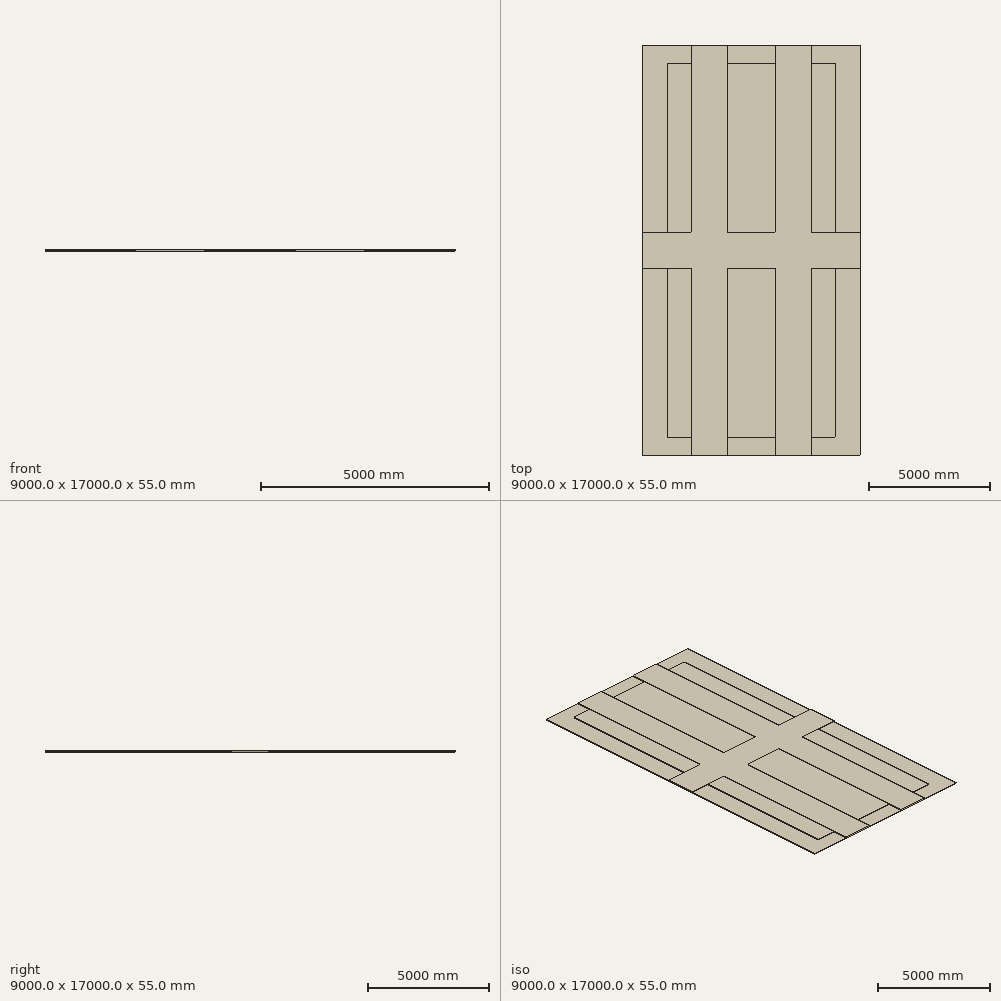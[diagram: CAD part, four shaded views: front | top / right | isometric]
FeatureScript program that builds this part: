
annotation { "Feature Type Name" : "Feature", "Feature Type Description" : "" }
export const myFeature = defineFeature(function(context is Context, id is Id, definition is map)
    precondition{}
    {
        {
            var Q0;
            Q0=qCreatedBy(makeId("Top.planeOp"),FACE);
            var sketch = newSketch(context, id + "F0", { "sketchPlane" : qUnion([Q0])});
            skLineSegment(sketch, "E0.bottom", {"start": v(0, 0) * mm, "end": v(-9000, 0) * mm});
            skLineSegment(sketch, "E0.top", {"start": v(0, 17000) * mm, "end": v(-9000, 17000) * mm});
            skLineSegment(sketch, "E0.left", {"start": v(0, 0) * mm, "end": v(0, 17000) * mm});
            skLineSegment(sketch, "E0.right", {"start": v(-9000, 0) * mm, "end": v(-9000, 17000) * mm});
            skSolve(sketch);
        }
        {
            var Q0;
            Q0=makeQuery(id+"F0.imprint","IMPRINT",FACE,{"disambiguationData":[TD([[makeQuery(id+"F0.imprint","IMPRINT",EDGE,{"derivedFrom":sQuery(id+"F0.wireOp",EDGE,"E0.bottom")}),-1.0]])]});
            extrude(context, id + "F1", {"entities" : qUnion([Q0]), "depth" : 25 * mm, "offsetDistance" : 25 * mm});
        }
        {
            var Q0;
            Q0=makeQuery(id+"F1.opExtrude","CAP_FACE",FACE,{"disambiguationData":[OSD([sQuery(id+"F0.wireOp",EDGE,"E0.bottom"),sQuery(id+"F0.wireOp",EDGE,"E0.top"),sQuery(id+"F0.wireOp",EDGE,"E0.left"),sQuery(id+"F0.wireOp",EDGE,"E0.right")])],"isStart":false});
            var sketch = newSketch(context, id + "F2", { "sketchPlane" : qUnion([Q0])});
            skLineSegment(sketch, "E1", {"start": v(0, 0) * mm, "end": v(-1000, 0) * mm});
            skLineSegment(sketch, "E2", {"start": v(-1000, 0) * mm, "end": v(-2000, 0) * mm});
            skLineSegment(sketch, "E3", {"start": v(-2000, 0) * mm, "end": v(-3500, 0) * mm});
            skLineSegment(sketch, "E4", {"start": v(-3500, 0) * mm, "end": v(-4500, 0) * mm});
            skLineSegment(sketch, "E5", {"start": v(-4500, 0) * mm, "end": v(-5500, 0) * mm});
            skLineSegment(sketch, "E6", {"start": v(-5500, 0) * mm, "end": v(-7000, 0) * mm});
            skLineSegment(sketch, "E7", {"start": v(-7000, 0) * mm, "end": v(-8000, 0) * mm});
            skLineSegment(sketch, "E8", {"start": v(-8000, 0) * mm, "end": v(-9000, 0) * mm});
            skLineSegment(sketch, "E9", {"start": v(-1000, 0) * mm, "end": v(-1000, 17000) * mm});
            skLineSegment(sketch, "E10", {"start": v(-2000, 0) * mm, "end": v(-2000, 17000) * mm});
            skLineSegment(sketch, "E11", {"start": v(-3500, 0) * mm, "end": v(-3500, 17000) * mm});
            skLineSegment(sketch, "E12", {"start": v(-4500, 0) * mm, "end": v(-4500, 17000) * mm});
            skLineSegment(sketch, "E13", {"start": v(-5500, 0) * mm, "end": v(-5500, 17000) * mm});
            skLineSegment(sketch, "E14", {"start": v(-7000, 0) * mm, "end": v(-7000, 17000) * mm});
            skLineSegment(sketch, "E15", {"start": v(-8000, 0) * mm, "end": v(-8000, 17000) * mm});
            skLineSegment(sketch, "E16", {"start": v(0, 0) * mm, "end": v(0, 750) * mm});
            skLineSegment(sketch, "E17", {"start": v(0, 750) * mm, "end": v(0, 7750) * mm});
            skLineSegment(sketch, "E18", {"start": v(0, 7750) * mm, "end": v(0, 9250) * mm});
            skLineSegment(sketch, "E19", {"start": v(0, 9250) * mm, "end": v(0, 16250) * mm});
            skLineSegment(sketch, "E20", {"start": v(0, 16250) * mm, "end": v(0, 17000) * mm});
            skLineSegment(sketch, "E21", {"start": v(0, 750) * mm, "end": v(-9000, 750) * mm});
            skLineSegment(sketch, "E22", {"start": v(0, 7750) * mm, "end": v(-9000, 7750) * mm});
            skLineSegment(sketch, "E23", {"start": v(0, 9250) * mm, "end": v(-9000, 9250) * mm});
            skLineSegment(sketch, "E24", {"start": v(0, 16250) * mm, "end": v(-9000, 16250) * mm});
            skSolve(sketch);
        }
        {
            var Q0;
            {var subQ0=sQuery(id+"F2.wireOp",EDGE,"E23");var subQ1=sQuery(id+"F2.wireOp",EDGE,"E14");var subQ2=makeQuery(id+"F2.imprint","INTERSECT",VERTEX,{"derivedFrom":[subQ1,subQ0]});Q0=makeQuery(id+"F2.imprint","IMPRINT",FACE,{"disambiguationData":[TD([[makeQuery(id+"F2.imprint","IMPRINT",EDGE,{"disambiguationData":[TD([[subQ2,-1.0]])],"derivedFrom":subQ1}),1.0]])]});}
            var Q1;
            {var subQ0=sQuery(id+"F2.wireOp",EDGE,"E23");var subQ1=sQuery(id+"F2.wireOp",EDGE,"E12");var subQ2=makeQuery(id+"F2.imprint","INTERSECT",VERTEX,{"derivedFrom":[subQ1,subQ0]});Q1=makeQuery(id+"F2.imprint","IMPRINT",FACE,{"disambiguationData":[TD([[makeQuery(id+"F2.imprint","IMPRINT",EDGE,{"disambiguationData":[TD([[subQ2,-1.0]])],"derivedFrom":subQ1}),1.0]])]});}
            var Q2;
            {var subQ0=sQuery(id+"F2.wireOp",EDGE,"E23");var subQ1=sQuery(id+"F2.wireOp",EDGE,"E11");var subQ2=makeQuery(id+"F2.imprint","INTERSECT",VERTEX,{"derivedFrom":[subQ1,subQ0]});Q2=makeQuery(id+"F2.imprint","IMPRINT",FACE,{"disambiguationData":[TD([[makeQuery(id+"F2.imprint","IMPRINT",EDGE,{"disambiguationData":[TD([[subQ2,-1.0]])],"derivedFrom":subQ1}),1.0]])]});}
            var Q3;
            {var subQ0=sQuery(id+"F2.wireOp",EDGE,"E23");var subQ1=sQuery(id+"F2.wireOp",EDGE,"E9");var subQ2=makeQuery(id+"F2.imprint","INTERSECT",VERTEX,{"derivedFrom":[subQ1,subQ0]});Q3=makeQuery(id+"F2.imprint","IMPRINT",FACE,{"disambiguationData":[TD([[makeQuery(id+"F2.imprint","IMPRINT",EDGE,{"disambiguationData":[TD([[subQ2,-1.0]])],"derivedFrom":subQ1}),1.0]])]});}
            var Q4;
            {var subQ0=sQuery(id+"F2.wireOp",EDGE,"E21");var subQ1=sQuery(id+"F2.wireOp",EDGE,"E14");var subQ2=makeQuery(id+"F2.imprint","INTERSECT",VERTEX,{"derivedFrom":[subQ1,subQ0]});Q4=makeQuery(id+"F2.imprint","IMPRINT",FACE,{"disambiguationData":[TD([[makeQuery(id+"F2.imprint","IMPRINT",EDGE,{"disambiguationData":[TD([[subQ2,-1.0]])],"derivedFrom":subQ1}),1.0]])]});}
            var Q5;
            {var subQ0=sQuery(id+"F2.wireOp",EDGE,"E21");var subQ1=sQuery(id+"F2.wireOp",EDGE,"E12");var subQ2=makeQuery(id+"F2.imprint","INTERSECT",VERTEX,{"derivedFrom":[subQ1,subQ0]});Q5=makeQuery(id+"F2.imprint","IMPRINT",FACE,{"disambiguationData":[TD([[makeQuery(id+"F2.imprint","IMPRINT",EDGE,{"disambiguationData":[TD([[subQ2,-1.0]])],"derivedFrom":subQ1}),1.0]])]});}
            var Q6;
            {var subQ0=sQuery(id+"F2.wireOp",EDGE,"E21");var subQ1=sQuery(id+"F2.wireOp",EDGE,"E11");var subQ2=makeQuery(id+"F2.imprint","INTERSECT",VERTEX,{"derivedFrom":[subQ1,subQ0]});Q6=makeQuery(id+"F2.imprint","IMPRINT",FACE,{"disambiguationData":[TD([[makeQuery(id+"F2.imprint","IMPRINT",EDGE,{"disambiguationData":[TD([[subQ2,-1.0]])],"derivedFrom":subQ1}),1.0]])]});}
            var Q7;
            {var subQ0=sQuery(id+"F2.wireOp",EDGE,"E21");var subQ1=sQuery(id+"F2.wireOp",EDGE,"E9");var subQ2=makeQuery(id+"F2.imprint","INTERSECT",VERTEX,{"derivedFrom":[subQ1,subQ0]});Q7=makeQuery(id+"F2.imprint","IMPRINT",FACE,{"disambiguationData":[TD([[makeQuery(id+"F2.imprint","IMPRINT",EDGE,{"disambiguationData":[TD([[subQ2,-1.0]])],"derivedFrom":subQ1}),1.0]])]});}
            extrude(context, id + "F3", {"entities" : qUnion([Q0, Q1, Q2, Q3, Q4, Q5, Q6, Q7]), "operationType" : NewBodyOperationType.ADD, "depth" : 25 * mm, "offsetDistance" : 25 * mm});
        }
        {
            var Q0;
            {var subQ0=sQuery(id+"F2.wireOp",EDGE,"E22");var subQ1=sQuery(id+"F2.wireOp",EDGE,"E14");var subQ2=makeQuery(id+"F2.imprint","INTERSECT",VERTEX,{"derivedFrom":[subQ1,subQ0]});Q0=makeQuery(id+"F2.imprint","IMPRINT",FACE,{"disambiguationData":[TD([[makeQuery(id+"F2.imprint","IMPRINT",EDGE,{"disambiguationData":[TD([[subQ2,-1.0]])],"derivedFrom":subQ1}),1.0]])]});}
            var Q1;
            {var subQ0=sQuery(id+"F2.wireOp",EDGE,"E22");var subQ1=sQuery(id+"F2.wireOp",EDGE,"E13");var subQ2=makeQuery(id+"F2.imprint","INTERSECT",VERTEX,{"derivedFrom":[subQ1,subQ0]});Q1=makeQuery(id+"F2.imprint","IMPRINT",FACE,{"disambiguationData":[TD([[makeQuery(id+"F2.imprint","IMPRINT",EDGE,{"disambiguationData":[TD([[subQ2,-1.0]])],"derivedFrom":subQ1}),1.0]])]});}
            var Q2;
            {var subQ0=sQuery(id+"F2.wireOp",EDGE,"E22");var subQ1=sQuery(id+"F2.wireOp",EDGE,"E12");var subQ2=makeQuery(id+"F2.imprint","INTERSECT",VERTEX,{"derivedFrom":[subQ1,subQ0]});Q2=makeQuery(id+"F2.imprint","IMPRINT",FACE,{"disambiguationData":[TD([[makeQuery(id+"F2.imprint","IMPRINT",EDGE,{"disambiguationData":[TD([[subQ2,-1.0]])],"derivedFrom":subQ1}),1.0]])]});}
            var Q3;
            {var subQ0=sQuery(id+"F2.wireOp",EDGE,"E22");var subQ1=sQuery(id+"F2.wireOp",EDGE,"E11");var subQ2=makeQuery(id+"F2.imprint","INTERSECT",VERTEX,{"derivedFrom":[subQ1,subQ0]});Q3=makeQuery(id+"F2.imprint","IMPRINT",FACE,{"disambiguationData":[TD([[makeQuery(id+"F2.imprint","IMPRINT",EDGE,{"disambiguationData":[TD([[subQ2,-1.0]])],"derivedFrom":subQ1}),1.0]])]});}
            var Q4;
            {var subQ0=sQuery(id+"F2.wireOp",EDGE,"E22");var subQ1=sQuery(id+"F2.wireOp",EDGE,"E10");var subQ2=makeQuery(id+"F2.imprint","INTERSECT",VERTEX,{"derivedFrom":[subQ1,subQ0]});Q4=makeQuery(id+"F2.imprint","IMPRINT",FACE,{"disambiguationData":[TD([[makeQuery(id+"F2.imprint","IMPRINT",EDGE,{"disambiguationData":[TD([[subQ2,-1.0]])],"derivedFrom":subQ1}),1.0]])]});}
            var Q5;
            {var subQ0=sQuery(id+"F2.wireOp",EDGE,"E22");var subQ1=sQuery(id+"F2.wireOp",EDGE,"E9");var subQ2=makeQuery(id+"F2.imprint","INTERSECT",VERTEX,{"derivedFrom":[subQ1,subQ0]});Q5=makeQuery(id+"F2.imprint","IMPRINT",FACE,{"disambiguationData":[TD([[makeQuery(id+"F2.imprint","IMPRINT",EDGE,{"disambiguationData":[TD([[subQ2,-1.0]])],"derivedFrom":subQ1}),1.0]])]});}
            var Q6;
            {var subQ5=sQuery(id+"F2.wireOp",EDGE,"E18");Q6=makeQuery(id+"F2.imprint","IMPRINT",FACE,{"disambiguationData":[TD([[makeQuery(id+"F2.imprint","IMPRINT",EDGE,{"derivedFrom":subQ5}),1.0]])]});}
            var Q7;
            {var subQ0=sQuery(id+"F2.wireOp",EDGE,"E22");var subQ1=sQuery(id+"F2.wireOp",EDGE,"E15");var subQ2=makeQuery(id+"F2.imprint","INTERSECT",VERTEX,{"derivedFrom":[subQ1,subQ0]});Q7=makeQuery(id+"F2.imprint","IMPRINT",FACE,{"disambiguationData":[TD([[makeQuery(id+"F2.imprint","IMPRINT",EDGE,{"disambiguationData":[TD([[subQ2,-1.0]])],"derivedFrom":subQ1}),1.0]])]});}
            var Q8;
            {var subQ0=sQuery(id+"F2.wireOp",EDGE,"E23");var subQ1=sQuery(id+"F2.wireOp",EDGE,"E13");var subQ2=makeQuery(id+"F2.imprint","INTERSECT",VERTEX,{"derivedFrom":[subQ1,subQ0]});Q8=makeQuery(id+"F2.imprint","IMPRINT",FACE,{"disambiguationData":[TD([[makeQuery(id+"F2.imprint","IMPRINT",EDGE,{"disambiguationData":[TD([[subQ2,-1.0]])],"derivedFrom":subQ1}),1.0]])]});}
            var Q9;
            {var subQ0=sQuery(id+"F2.wireOp",EDGE,"E23");var subQ1=sQuery(id+"F2.wireOp",EDGE,"E10");var subQ2=makeQuery(id+"F2.imprint","INTERSECT",VERTEX,{"derivedFrom":[subQ1,subQ0]});Q9=makeQuery(id+"F2.imprint","IMPRINT",FACE,{"disambiguationData":[TD([[makeQuery(id+"F2.imprint","IMPRINT",EDGE,{"disambiguationData":[TD([[subQ2,-1.0]])],"derivedFrom":subQ1}),1.0]])]});}
            var Q10;
            {var subQ0=sQuery(id+"F2.wireOp",EDGE,"E13");var subQ1=makeQuery(id+"F1.opExtrude","CAP_EDGE",EDGE,{"disambiguationData":[OSD([sQuery(id+"F0.wireOp",EDGE,"E0.top")])],"isStart":false});var subQ2=makeQuery(id+"F2.imprint","INTERSECT",VERTEX,{"derivedFrom":[subQ1,subQ0]});Q10=makeQuery(id+"F2.imprint","IMPRINT",FACE,{"disambiguationData":[TD([[makeQuery(id+"F2.imprint","IMPRINT",EDGE,{"disambiguationData":[TD([[subQ2,1.0]])],"derivedFrom":subQ0}),1.0]])]});}
            var Q11;
            {var subQ0=sQuery(id+"F2.wireOp",EDGE,"E10");var subQ1=makeQuery(id+"F1.opExtrude","CAP_EDGE",EDGE,{"disambiguationData":[OSD([sQuery(id+"F0.wireOp",EDGE,"E0.top")])],"isStart":false});var subQ2=makeQuery(id+"F2.imprint","INTERSECT",VERTEX,{"derivedFrom":[subQ1,subQ0]});Q11=makeQuery(id+"F2.imprint","IMPRINT",FACE,{"disambiguationData":[TD([[makeQuery(id+"F2.imprint","IMPRINT",EDGE,{"disambiguationData":[TD([[subQ2,1.0]])],"derivedFrom":subQ0}),1.0]])]});}
            var Q12;
            {var subQ0=sQuery(id+"F2.wireOp",EDGE,"E21");var subQ1=sQuery(id+"F2.wireOp",EDGE,"E13");var subQ2=makeQuery(id+"F2.imprint","INTERSECT",VERTEX,{"derivedFrom":[subQ1,subQ0]});Q12=makeQuery(id+"F2.imprint","IMPRINT",FACE,{"disambiguationData":[TD([[makeQuery(id+"F2.imprint","IMPRINT",EDGE,{"disambiguationData":[TD([[subQ2,-1.0]])],"derivedFrom":subQ1}),1.0]])]});}
            var Q13;
            {var subQ0=sQuery(id+"F2.wireOp",EDGE,"E21");var subQ1=sQuery(id+"F2.wireOp",EDGE,"E10");var subQ2=makeQuery(id+"F2.imprint","INTERSECT",VERTEX,{"derivedFrom":[subQ1,subQ0]});Q13=makeQuery(id+"F2.imprint","IMPRINT",FACE,{"disambiguationData":[TD([[makeQuery(id+"F2.imprint","IMPRINT",EDGE,{"disambiguationData":[TD([[subQ2,-1.0]])],"derivedFrom":subQ1}),1.0]])]});}
            var Q14;
            {var subQ0=sQuery(id+"F2.wireOp",EDGE,"E6");Q14=makeQuery(id+"F2.imprint","IMPRINT",FACE,{"disambiguationData":[TD([[makeQuery(id+"F2.imprint","IMPRINT",EDGE,{"derivedFrom":subQ0}),-1.0]])]});}
            var Q15;
            {var subQ0=sQuery(id+"F2.wireOp",EDGE,"E3");Q15=makeQuery(id+"F2.imprint","IMPRINT",FACE,{"disambiguationData":[TD([[makeQuery(id+"F2.imprint","IMPRINT",EDGE,{"derivedFrom":subQ0}),-1.0]])]});}
            extrude(context, id + "F4", {"entities" : qUnion([Q0, Q1, Q2, Q3, Q4, Q5, Q6, Q7, Q8, Q9, Q10, Q11, Q12, Q13, Q14, Q15]), "operationType" : NewBodyOperationType.ADD, "depth" : 30 * mm, "offsetDistance" : 25 * mm});
        }
    });
